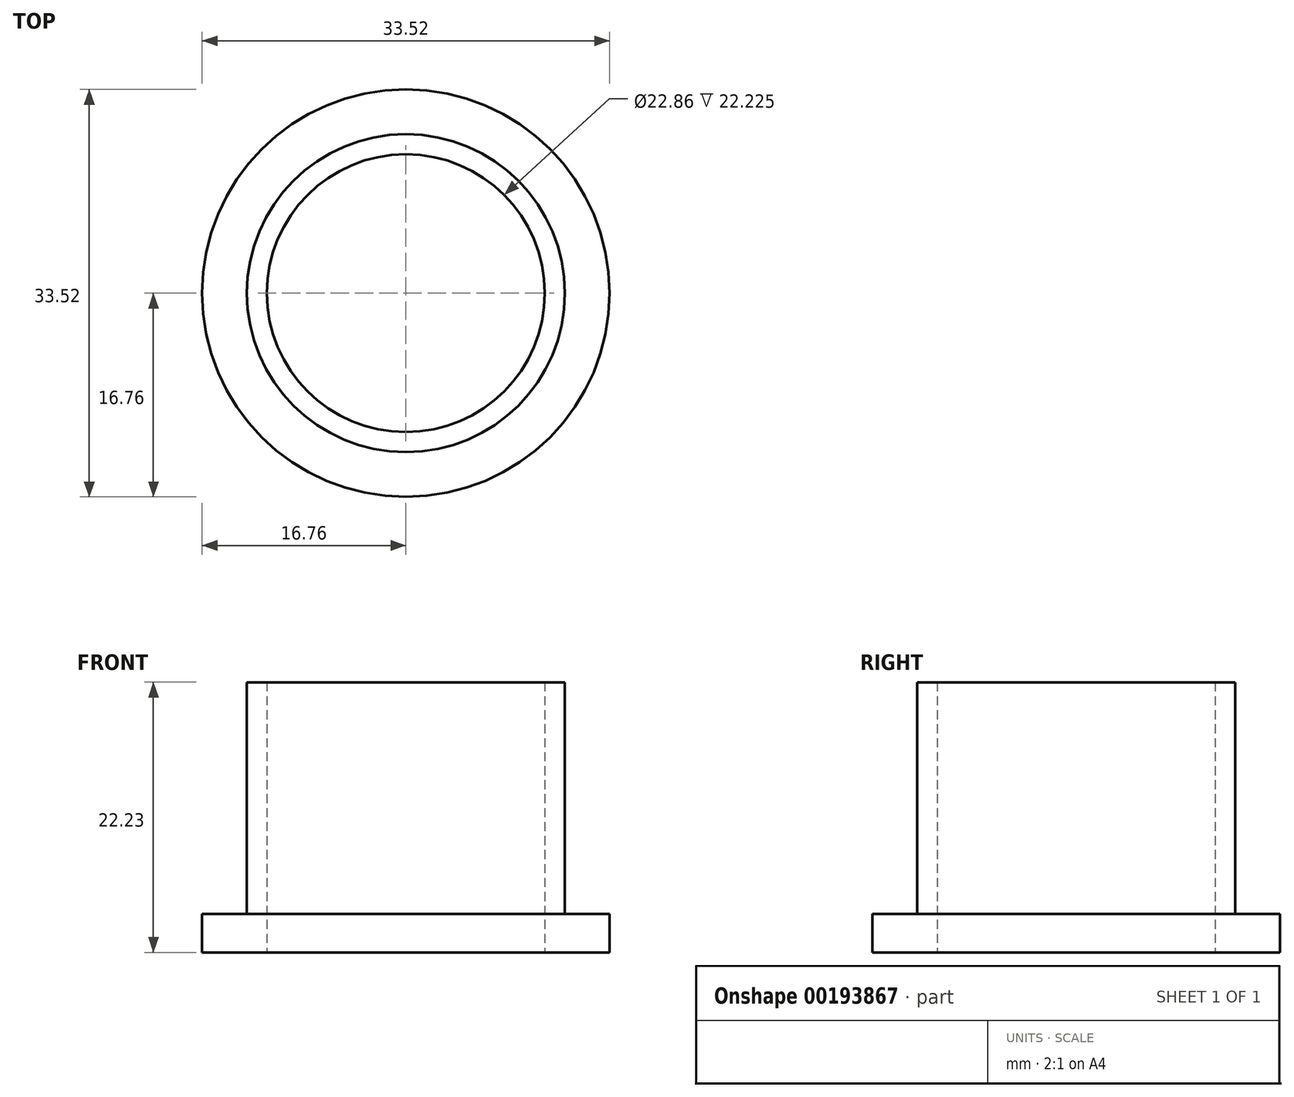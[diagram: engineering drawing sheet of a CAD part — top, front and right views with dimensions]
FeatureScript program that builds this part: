
annotation { "Feature Type Name" : "Feature", "Feature Type Description" : "" }
export const myFeature = defineFeature(function(context is Context, id is Id, definition is map)
    precondition{}
    {
        {
            var Q0;
            Q0=qCreatedBy(makeId("Top.planeOp"),FACE);
            var sketch = newSketch(context, id + "F0", { "sketchPlane" : qUnion([Q0])});
            skCircle(sketch, "E0", {"center": v(0, 0) * mm, "radius": 16.76 * mm});
            skCircle(sketch, "E1", {"center": v(0, 0) * mm, "radius": 11.43 * mm});
            skSolve(sketch);
        }
        {
            var Q0;
            Q0=makeQuery(id+"F0.imprint","IMPRINT",FACE,{"disambiguationData":[TD([[makeQuery(id+"F0.imprint","IMPRINT",EDGE,{"derivedFrom":sQuery(id+"F0.wireOp",EDGE,"E0")}),1.0]])]});
            extrude(context, id + "F1", {"entities" : qUnion([Q0]), "depth" : 3.17 * mm});
        }
        {
            var Q0;
            Q0=makeQuery(id+"F1.opExtrude","CAP_FACE",FACE,{"disambiguationData":[OSD([sQuery(id+"F0.wireOp",EDGE,"E0")])],"isStart":false});
            var sketch = newSketch(context, id + "F2", { "sketchPlane" : qUnion([Q0])});
            skCircle(sketch, "E2", {"center": v(0, 0) * mm, "radius": 11.43 * mm});
            skSolve(sketch);
        }
        {
            var Q0;
            Q0=makeQuery(id+"F2.imprint","IMPRINT",FACE,{"disambiguationData":[TD([[makeQuery(id+"F2.imprint","IMPRINT",EDGE,{"derivedFrom":sQuery(id+"F2.wireOp",EDGE,"E2")}),-1.0]])]});
            var sketch = newSketch(context, id + "F3", { "sketchPlane" : qUnion([Q0])});
            skCircle(sketch, "E3", {"center": v(0, 0) * mm, "radius": 13.08 * mm});
            skSolve(sketch);
        }
        {
            var Q0;
            Q0=makeQuery(id+"F3.imprint","IMPRINT",FACE,{"disambiguationData":[TD([[makeQuery(id+"F3.imprint","IMPRINT",EDGE,{"derivedFrom":sQuery(id+"F3.wireOp",EDGE,"E3")}),1.0]])]});
            extrude(context, id + "F4", {"entities" : qUnion([Q0]), "operationType" : NewBodyOperationType.ADD, "depth" : 19.05 * mm});
        }
    });
